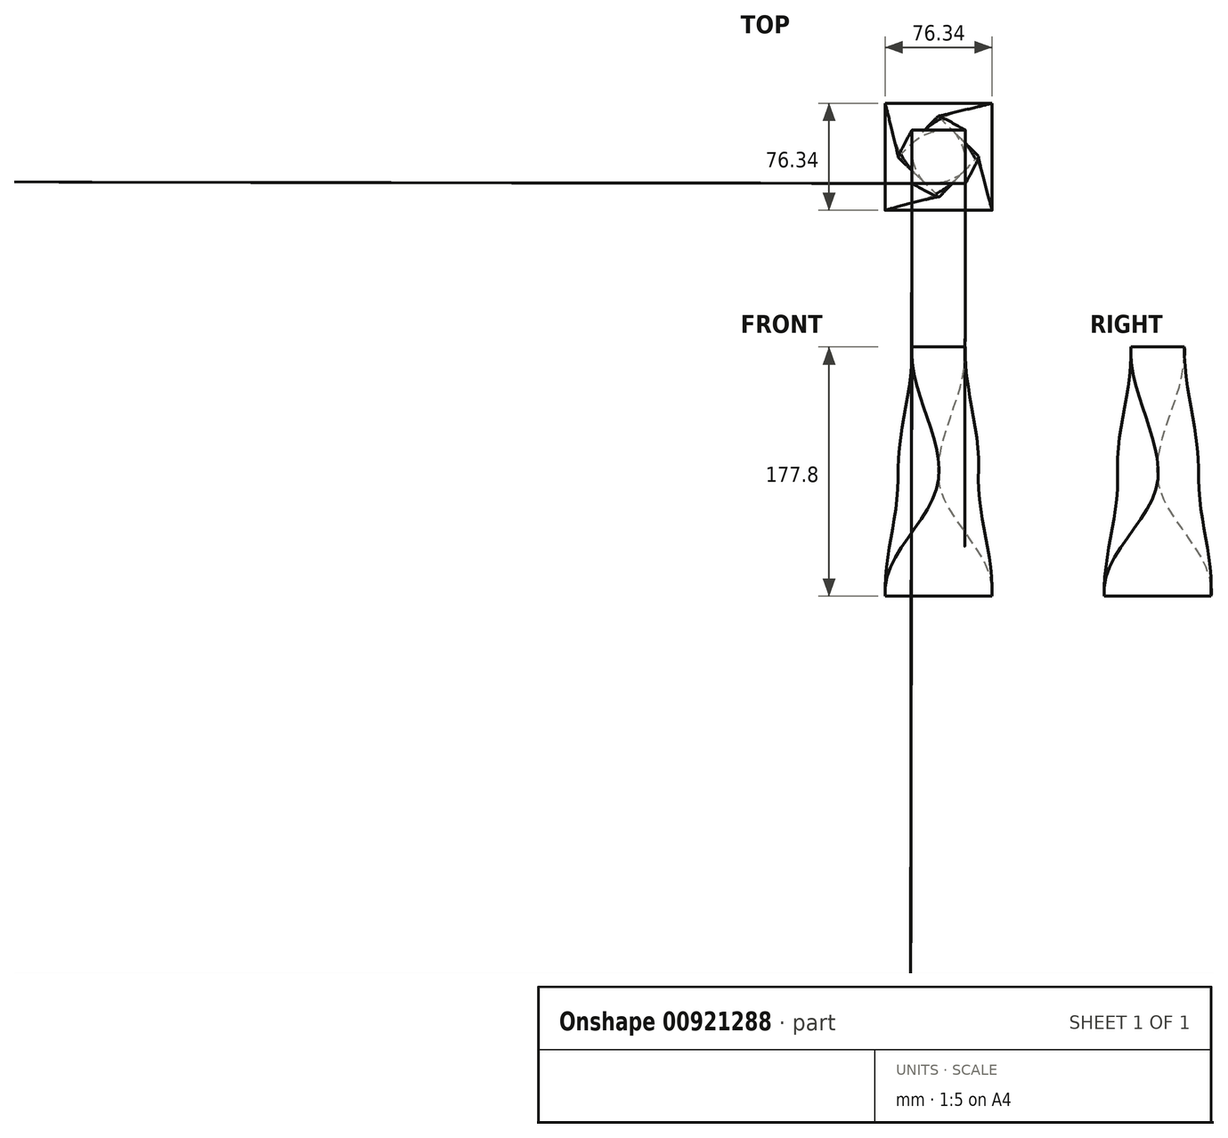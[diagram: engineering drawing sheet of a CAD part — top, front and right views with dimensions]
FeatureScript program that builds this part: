
annotation { "Feature Type Name" : "Feature", "Feature Type Description" : "" }
export const myFeature = defineFeature(function(context is Context, id is Id, definition is map)
    precondition{}
    {
        {
            var Q0;
            Q0=qCreatedBy(makeId("Top.planeOp"),FACE);
            var sketch = newSketch(context, id + "F0", { "sketchPlane" : qUnion([Q0])});
            skLineSegment(sketch, "E0.bottom", {"start": v(38.1, -38.1) * mm, "end": v(-38.1, -38.1) * mm});
            skLineSegment(sketch, "E0.top", {"start": v(38.1, 38.1) * mm, "end": v(-38.1, 38.1) * mm});
            skLineSegment(sketch, "E0.left", {"start": v(38.1, -38.1) * mm, "end": v(38.1, 38.1) * mm});
            skLineSegment(sketch, "E0.right", {"start": v(-38.1, -38.1) * mm, "end": v(-38.1, 38.1) * mm});
            skPoint(sketch, "E0.middle", {"position": v(0, 0) * mm});
            skSolve(sketch);
        }
        {
            var Q0;
            Q0=qCreatedBy(makeId("Top.planeOp"),FACE);
            cPlane(context, id + "F1", {"entities" : qUnion([Q0]), "cplaneType" : CPlaneType.OFFSET, "offset" : 6.35 * mm, "width" : 152.4 * mm, "height" : 152.4 * mm});
        }
        {
            var Q0;
            Q0=qCreatedBy(id+"F1.planeOp",FACE);
            var sketch = newSketch(context, id + "F2", { "sketchPlane" : qUnion([Q0])});
            skLineSegment(sketch, "E1.bottom", {"start": v(38.1, -38.1) * mm, "end": v(-38.1, -38.1) * mm});
            skLineSegment(sketch, "E1.top", {"start": v(38.1, 38.1) * mm, "end": v(-38.1, 38.1) * mm});
            skLineSegment(sketch, "E1.left", {"start": v(38.1, -38.1) * mm, "end": v(38.1, 38.1) * mm});
            skLineSegment(sketch, "E1.right", {"start": v(-38.1, -38.1) * mm, "end": v(-38.1, 38.1) * mm});
            skPoint(sketch, "E1.middle", {"position": v(0, 0) * mm});
            skSolve(sketch);
        }
        {
            var Q0;
            Q0=qCreatedBy(id+"F1.planeOp",FACE);
            cPlane(context, id + "F3", {"entities" : qUnion([Q0]), "cplaneType" : CPlaneType.OFFSET, "offset" : 76.2 * mm, "width" : 152.4 * mm, "height" : 152.4 * mm});
        }
        {
            var Q0;
            Q0=qCreatedBy(id+"F3.planeOp",FACE);
            var sketch = newSketch(context, id + "F4", { "sketchPlane" : qUnion([Q0])});
            skLineSegment(sketch, "E2.0", {"start": v(28.4, 0.03) * mm, "end": v(-0.03, 29.04) * mm});
            skLineSegment(sketch, "E3.0", {"start": v(-0.03, 29.04) * mm, "end": v(-28.84, 0.03) * mm});
            skLineSegment(sketch, "E4.0", {"start": v(-28.84, 0.03) * mm, "end": v(-0.03, -28.6) * mm});
            skLineSegment(sketch, "E5.0", {"start": v(-0.03, -28.6) * mm, "end": v(28.4, 0.03) * mm});
            skPoint(sketch, "E6.orphan", {"position": v(37.32, 0) * mm});
            skPoint(sketch, "E7.start.orphan", {"position": v(0, 38.08) * mm});
            skPoint(sketch, "E8.start.orphan", {"position": v(0, -37.57) * mm});
            skPoint(sketch, "E9.start.orphan", {"position": v(-37.82, 0) * mm});
            skSolve(sketch);
        }
        {
            var Q0;
            Q0=qCreatedBy(id+"F3.planeOp",FACE);
            cPlane(context, id + "F5", {"entities" : qUnion([Q0]), "cplaneType" : CPlaneType.OFFSET, "offset" : 12.7 * mm, "width" : 152.4 * mm, "height" : 152.4 * mm});
        }
        {
            var Q0;
            Q0=qCreatedBy(id+"F5.planeOp",FACE);
            var sketch = newSketch(context, id + "F6", { "sketchPlane" : qUnion([Q0])});
            skLineSegment(sketch, "E10.0", {"start": v(28.53, -0.1) * mm, "end": v(0.1, 28.9) * mm});
            skLineSegment(sketch, "E11.0", {"start": v(-28.72, -0.1) * mm, "end": v(0.1, -28.72) * mm});
            skLineSegment(sketch, "E12.0", {"start": v(0.1, -28.72) * mm, "end": v(28.53, -0.1) * mm});
            skLineSegment(sketch, "E13.0", {"start": v(0.1, 28.9) * mm, "end": v(-28.72, -0.1) * mm});
            skLineSegment(sketch, "E14.trimOffspring", {"start": v(-4.35, 33.44) * mm, "end": v(-4.4, 33.5) * mm});
            skSolve(sketch);
        }
        {
            var Q0;
            Q0=qCreatedBy(id+"F5.planeOp",FACE);
            cPlane(context, id + "F7", {"entities" : qUnion([Q0]), "cplaneType" : CPlaneType.OFFSET, "offset" : 76.2 * mm, "width" : 152.4 * mm, "height" : 152.4 * mm});
        }
        {
            var Q0;
            Q0=qCreatedBy(id+"F7.planeOp",FACE);
            var sketch = newSketch(context, id + "F8", { "sketchPlane" : qUnion([Q0])});
            skPoint(sketch, "E15.middle", {"position": v(0, 0) * mm});
            skPoint(sketch, "E15.left.end.orphan", {"position": v(22.53, 22.53) * mm});
            skPoint(sketch, "E15.bottom.start.orphan", {"position": v(22.53, -22.53) * mm});
            skPoint(sketch, "E15.right.end.orphan", {"position": v(-22.53, 22.53) * mm});
            skPoint(sketch, "E15.right.start.orphan", {"position": v(-22.53, -22.53) * mm});
            skLineSegment(sketch, "E16.bottom", {"start": v(19.05, -19.05) * mm, "end": v(-19.05, -19.05) * mm});
            skLineSegment(sketch, "E16.top", {"start": v(19.05, 19.05) * mm, "end": v(-19.05, 19.05) * mm});
            skLineSegment(sketch, "E16.left", {"start": v(19.05, -19.05) * mm, "end": v(19.05, 19.05) * mm});
            skLineSegment(sketch, "E16.right", {"start": v(-19.05, -19.05) * mm, "end": v(-19.05, 19.05) * mm});
            skSolve(sketch);
        }
        {
            var Q0;
            Q0=qCreatedBy(id+"F7.planeOp",FACE);
            cPlane(context, id + "F9", {"entities" : qUnion([Q0]), "cplaneType" : CPlaneType.OFFSET, "offset" : 6.35 * mm, "width" : 152.4 * mm, "height" : 152.4 * mm});
        }
        {
            var Q0;
            Q0=qCreatedBy(id+"F9.planeOp",FACE);
            var sketch = newSketch(context, id + "F10", { "sketchPlane" : qUnion([Q0])});
            skPoint(sketch, "E17.middle", {"position": v(0, 0) * mm});
            skPoint(sketch, "E17.left.end.orphan", {"position": v(27.29, 27.29) * mm});
            skPoint(sketch, "E17.bottom.start.orphan", {"position": v(27.29, -27.29) * mm});
            skPoint(sketch, "E17.right.end.orphan", {"position": v(-27.29, 27.29) * mm});
            skPoint(sketch, "E17.right.start.orphan", {"position": v(-27.29, -27.29) * mm});
            skLineSegment(sketch, "E18.bottom", {"start": v(19.05, -19.05) * mm, "end": v(-19.05, -19.05) * mm});
            skLineSegment(sketch, "E18.top", {"start": v(19.05, 19.05) * mm, "end": v(-19.05, 19.05) * mm});
            skLineSegment(sketch, "E18.left", {"start": v(19.05, -19.05) * mm, "end": v(19.05, 19.05) * mm});
            skLineSegment(sketch, "E18.right", {"start": v(-19.05, -19.05) * mm, "end": v(-19.05, 19.05) * mm});
            skSolve(sketch);
        }
        {
            var Q0;
            Q0=makeQuery(id+"F0.imprint","IMPRINT",FACE,{"disambiguationData":[TD([[makeQuery(id+"F0.imprint","IMPRINT",EDGE,{"derivedFrom":sQuery(id+"F0.wireOp",EDGE,"E0.bottom")}),-1.0]])]});
            var Q1;
            Q1=makeQuery(id+"F2.imprint","IMPRINT",FACE,{"disambiguationData":[TD([[makeQuery(id+"F2.imprint","IMPRINT",EDGE,{"derivedFrom":sQuery(id+"F2.wireOp",EDGE,"E1.bottom")}),-1.0]])]});
            var Q2;
            Q2=makeQuery(id+"F4.imprint","IMPRINT",FACE,{"disambiguationData":[TD([[makeQuery(id+"F4.imprint","IMPRINT",EDGE,{"derivedFrom":sQuery(id+"F4.wireOp",EDGE,"E2.0")}),1.0]])]});
            var Q3;
            Q3=makeQuery(id+"F6.imprint","IMPRINT",FACE,{"disambiguationData":[TD([[makeQuery(id+"F6.imprint","IMPRINT",EDGE,{"derivedFrom":sQuery(id+"F6.wireOp",EDGE,"E10.0")}),1.0]])]});
            var Q4;
            Q4=makeQuery(id+"F8.imprint","IMPRINT",FACE,{"disambiguationData":[TD([[makeQuery(id+"F8.imprint","IMPRINT",EDGE,{"derivedFrom":sQuery(id+"F8.wireOp",EDGE,"E16.bottom")}),-1.0]])]});
            var Q5;
            Q5=makeQuery(id+"F10.imprint","IMPRINT",FACE,{"disambiguationData":[TD([[makeQuery(id+"F10.imprint","IMPRINT",EDGE,{"derivedFrom":sQuery(id+"F10.wireOp",EDGE,"E18.bottom")}),-1.0]])]});
            loft(context, id + "F11", {"sheetProfilesArray" : [{ "sheetProfileEntities" : qUnion([Q0]) }, { "sheetProfileEntities" : qUnion([Q1]) }, { "sheetProfileEntities" : qUnion([Q2]) }, { "sheetProfileEntities" : qUnion([Q3]) }, { "sheetProfileEntities" : qUnion([Q4]) }, { "sheetProfileEntities" : qUnion([Q5]) }]});
        }
    });
